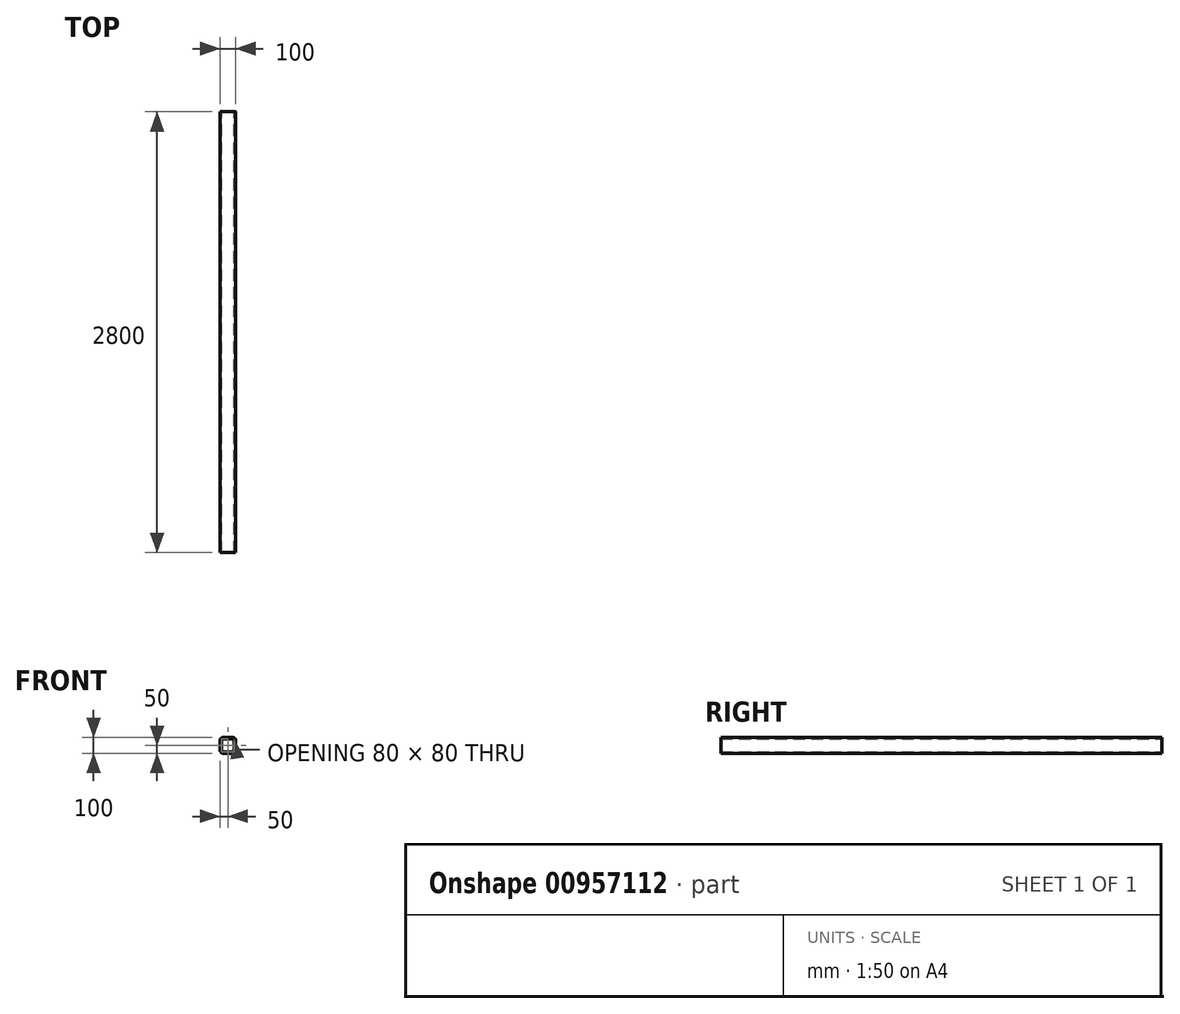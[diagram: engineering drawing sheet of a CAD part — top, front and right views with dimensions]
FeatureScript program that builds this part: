
annotation { "Feature Type Name" : "Feature", "Feature Type Description" : "" }
export const myFeature = defineFeature(function(context is Context, id is Id, definition is map)
    precondition{}
    {
        {
            var Q0;
            Q0=qCreatedBy(makeId("Front.planeOp"),FACE);
            var sketch = newSketch(context, id + "F0", { "sketchPlane" : qUnion([Q0])});
            skLineSegment(sketch, "E0.bottom", {"start": v(-30, -50) * mm, "end": v(30, -50) * mm});
            skLineSegment(sketch, "E0.top", {"start": v(-30, 50) * mm, "end": v(30, 50) * mm});
            skLineSegment(sketch, "E0.left", {"start": v(-50, -30) * mm, "end": v(-50, 30) * mm});
            skLineSegment(sketch, "E0.right", {"start": v(50, -30) * mm, "end": v(50, 30) * mm});
            skPoint(sketch, "E0.middle", {"position": v(0, 0) * mm});
            skPoint(sketch, "E1.visualSharp", {"position": v(-50, 50) * mm});
            skArc(sketch, "E2.filletArc", {"start": v(-30, 50) * mm, "mid": v(-44.14, 44.14) * mm, "end": v(-50, 30) * mm});
            skPoint(sketch, "E3.visualSharp", {"position": v(50, 50) * mm});
            skArc(sketch, "E3.filletArc", {"start": v(50, 30) * mm, "mid": v(44.14, 44.14) * mm, "end": v(30, 50) * mm});
            skPoint(sketch, "E4.visualSharp", {"position": v(50, -50) * mm});
            skArc(sketch, "E4.filletArc", {"start": v(30, -50) * mm, "mid": v(44.14, -44.14) * mm, "end": v(50, -30) * mm});
            skPoint(sketch, "E5.visualSharp", {"position": v(-50, -50) * mm});
            skArc(sketch, "E5.filletArc", {"start": v(-50, -30) * mm, "mid": v(-44.14, -44.14) * mm, "end": v(-30, -50) * mm});
            skLineSegment(sketch, "E6.bottom", {"start": v(-30, 40) * mm, "end": v(30, 40) * mm});
            skLineSegment(sketch, "E6.top", {"start": v(-30, -40) * mm, "end": v(30, -40) * mm});
            skLineSegment(sketch, "E6.left", {"start": v(-40, 30) * mm, "end": v(-40, -30) * mm});
            skLineSegment(sketch, "E6.right", {"start": v(40, 30) * mm, "end": v(40, -30) * mm});
            skPoint(sketch, "E7.visualSharp", {"position": v(-40, 40) * mm});
            skArc(sketch, "E7.filletArc", {"start": v(-30, 40) * mm, "mid": v(-37.07, 37.07) * mm, "end": v(-40, 30) * mm});
            skPoint(sketch, "E8.visualSharp", {"position": v(-40, -40) * mm});
            skArc(sketch, "E8.filletArc", {"start": v(-40, -30) * mm, "mid": v(-37.07, -37.07) * mm, "end": v(-30, -40) * mm});
            skPoint(sketch, "E9.visualSharp", {"position": v(40, 40) * mm});
            skArc(sketch, "E9.filletArc", {"start": v(40, 30) * mm, "mid": v(37.07, 37.07) * mm, "end": v(30, 40) * mm});
            skPoint(sketch, "E10.visualSharp", {"position": v(40, -40) * mm});
            skArc(sketch, "E10.filletArc", {"start": v(30, -40) * mm, "mid": v(37.07, -37.07) * mm, "end": v(40, -30) * mm});
            skSolve(sketch);
        }
        {
            var Q0;
            Q0 = qSketchRegion(id + "F0", true);
            extrude(context, id + "F1", {"entities" : qUnion([Q0]), "depth" : 2800 * mm, "offsetDistance" : 25 * mm});
        }
    });
